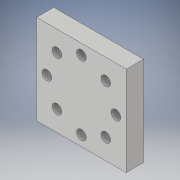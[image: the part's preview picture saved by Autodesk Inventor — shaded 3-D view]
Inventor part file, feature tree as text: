
AUTODESK INVENTOR PART (.ipt)
format: ipt  version: 2017 (Build 210142000, 142)  size: 115,200 bytes
history: native  units: in
note: dims shown in document units (in); Inventor stores cm internally (conversion verified against a paired STEP export)
features: sketch x3, extrude x1, hole x1
ambient origin geometry x8: Origin, YZ Plane, XZ Plane, XY Plane, X Axis, Y Axis, Z Axis, Center Point
bodies: Solid1 (feature_tree)
feature tree (5):
  extrude  "Extrusion1"  Depth=1.0in
  hole  "Hole1"  [1 undecoded]
  sketch  "Sketch3"  dims[d5=0.385in d6=0.107in d7=0.75in d8=0.375in d9=0.25in d10=0.5635in d11=1.0in d12=0.8108in d13=3.1496in d15=360.0deg]
  sketch  "Sketch1"  dims[d0=1.0in d1=1.0in]
  sketch  "Sketch2"  dims[d2=0.192in d3=0.0in d4=0.5in]
note: 1 required parameter value undecoded (feature->parameter linkage not recoverable at this tier; creation-order binding heuristic only, values carry confidence <= 0.55)
